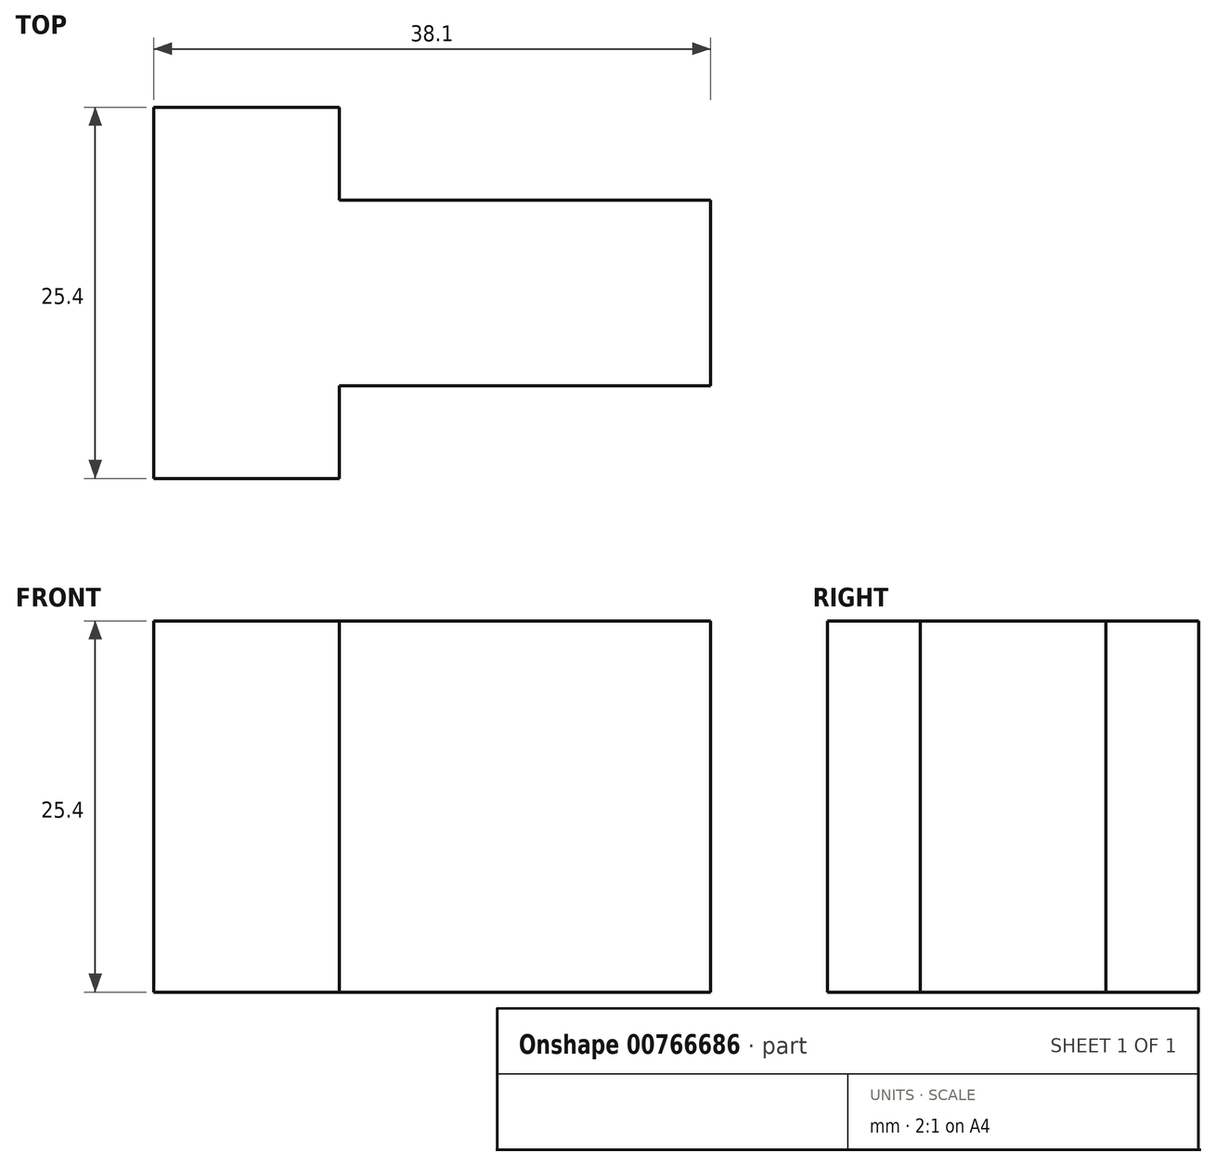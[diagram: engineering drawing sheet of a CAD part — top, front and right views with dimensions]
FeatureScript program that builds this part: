
annotation { "Feature Type Name" : "Feature", "Feature Type Description" : "" }
export const myFeature = defineFeature(function(context is Context, id is Id, definition is map)
    precondition{}
    {
        {
            var Q0;
            Q0=qCreatedBy(makeId("Top.planeOp"),FACE);
            var sketch = newSketch(context, id + "F0", { "sketchPlane" : qUnion([Q0])});
            skLineSegment(sketch, "E0", {"start": v(0, 0) * mm, "end": v(12.7, 0) * mm});
            skLineSegment(sketch, "E1", {"start": v(12.7, 0) * mm, "end": v(12.7, 6.35) * mm});
            skLineSegment(sketch, "E2", {"start": v(12.7, 6.35) * mm, "end": v(38.1, 6.35) * mm});
            skLineSegment(sketch, "E3", {"start": v(38.1, 6.35) * mm, "end": v(38.1, 19.05) * mm});
            skLineSegment(sketch, "E4", {"start": v(38.1, 19.05) * mm, "end": v(12.7, 19.05) * mm});
            skLineSegment(sketch, "E5", {"start": v(12.7, 19.05) * mm, "end": v(12.7, 25.4) * mm});
            skLineSegment(sketch, "E6", {"start": v(12.7, 25.4) * mm, "end": v(0, 25.4) * mm});
            skLineSegment(sketch, "E7", {"start": v(0, 0) * mm, "end": v(0, 25.4) * mm});
            skSolve(sketch);
        }
        {
            var Q0;
            Q0=makeQuery(id+"F0.imprint","IMPRINT",FACE,{"disambiguationData":[TD([[makeQuery(id+"F0.imprint","IMPRINT",EDGE,{"derivedFrom":sQuery(id+"F0.wireOp",EDGE,"E0")}),1.0]])]});
            extrude(context, id + "F1", {"entities" : qUnion([Q0]), "depth" : 25.4 * mm, "offsetDistance" : 25.4 * mm});
        }
    });
